# Revit family: xTowel_Bar-American_Standard-Studio_S-7105_Series
name_source: partatom
category: Specialty Equipment
revit_build: Autodesk Revit 2014 (Build: 20130308_1515(x64)
units: mm (PartAtom-declared; Revit-internal decimal feet)

## types (2) — shared parameters
Assembly Code = C1030220
Default Elevation = 48"
Finish = Metal-American Standard-002-Polished Chrome
Height = 2"
Installation Type = Wall Mount
Manufacturer = American Standard
Material = Metal-American Standard-002-Polished Chrome
Price = Prices may vary. Please consult Manufacturer Representative for most up-to-date price list.
Product Documentation Link = https://www.americanstandard-us.com
Product Page URL = https://www.americanstandard-us.com
URL = https://www.americanstandard-us.com
Warranty Information = One Year General Product Warranty
Width = 3 7/8"

## per-type parameters (varying)
| type | Description | Length | Specification |
| 7105.018 | Studio S 18" Towel Bar | 18" | Studio S 18" Towel Bar shall feature metal construction. Rod shall be brass. Shall feature concealed mounting with no exposed set screws. |
| 7105.024 | Studio S 24" Towel Bar | 24" | Studio S 24" Towel Bar shall feature metal construction. Rod shall be brass. Shall feature concealed mounting with no exposed set screws. |

note: column(s) folded — value = type name in every type: Model

## geometry (parser evidence)
native form markers: Sweep x3
no freeform markers — native parametric forms only
